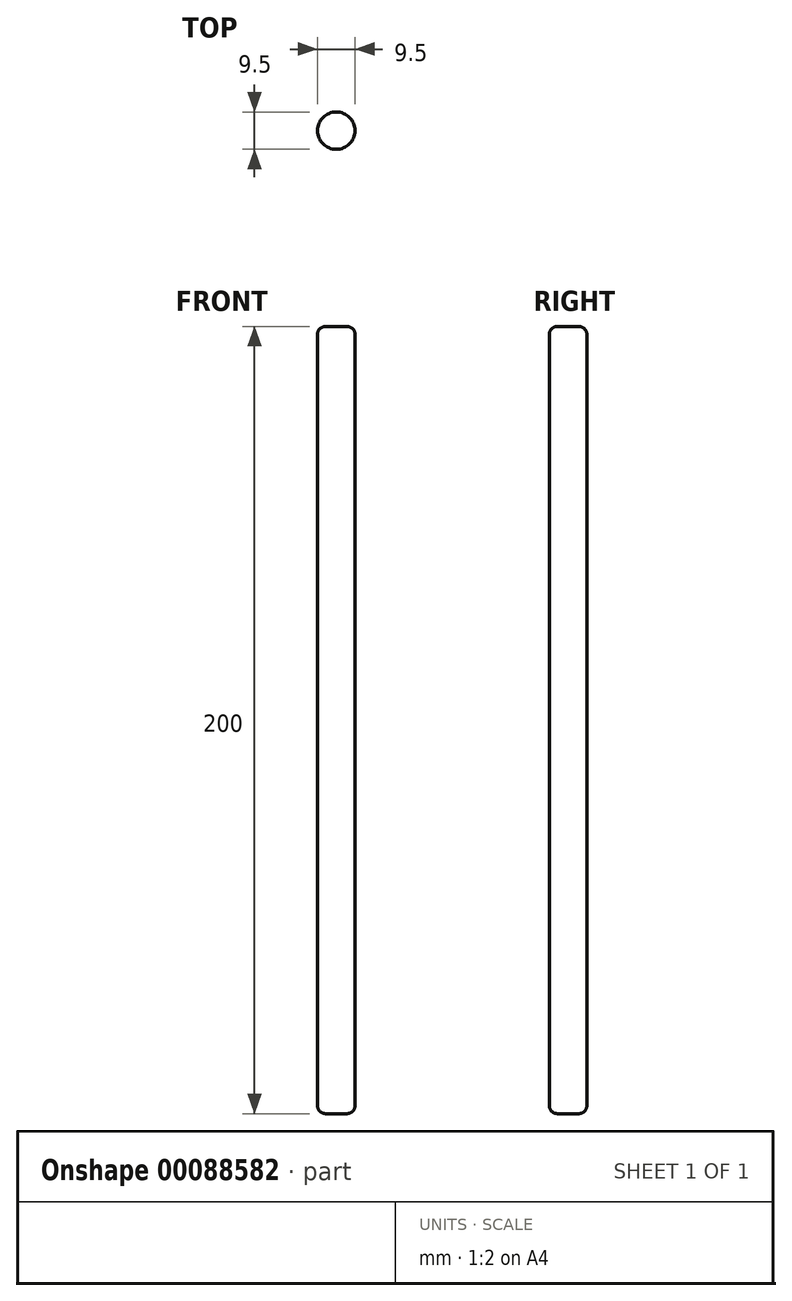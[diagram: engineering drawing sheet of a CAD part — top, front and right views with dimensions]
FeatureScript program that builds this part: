
annotation { "Feature Type Name" : "Feature", "Feature Type Description" : "" }
export const myFeature = defineFeature(function(context is Context, id is Id, definition is map)
    precondition{}
    {
        {
            var Q0;
            Q0=qCreatedBy(makeId("Top.planeOp"),FACE);
            var sketch = newSketch(context, id + "F0", { "sketchPlane" : qUnion([Q0])});
            skCircle(sketch, "E0", {"center": v(0, 0) * mm, "radius": 4.75 * mm});
            skSolve(sketch);
        }
        {
            var Q0;
            Q0=qSketchRegion(id+"F0",true);
            extrude(context, id + "F1", {"entities" : qUnion([Q0]), "depth" : 200 * mm});
        }
        {
            var Q0;
            Q0=qCreatedBy(makeId("Front.planeOp"),FACE);
            var sketch = newSketch(context, id + "F2", { "sketchPlane" : qUnion([Q0])});
            skCircle(sketch, "E1", {"center": v(0, 8.4) * mm, "radius": 3.1 * mm});
            skSolve(sketch);
        }
        {
            var Q0;
            Q0=makeQuery(id+"F1.opExtrude","CAP_EDGE",EDGE,{"disambiguationData":[OSD([sQuery(id+"F0.wireOp",EDGE,"E0")])],"isStart":true});
            var Q1;
            Q1=makeQuery(id+"F1.opExtrude","CAP_EDGE",EDGE,{"disambiguationData":[OSD([sQuery(id+"F0.wireOp",EDGE,"E0")])],"isStart":false});
            fillet(context, id + "F3", {"entities" : qUnion([Q0, Q1]), "radius" : 2 * mm, "tangentPropagation" : true, "allowEdgeOverflow" : false});
        }
    });
